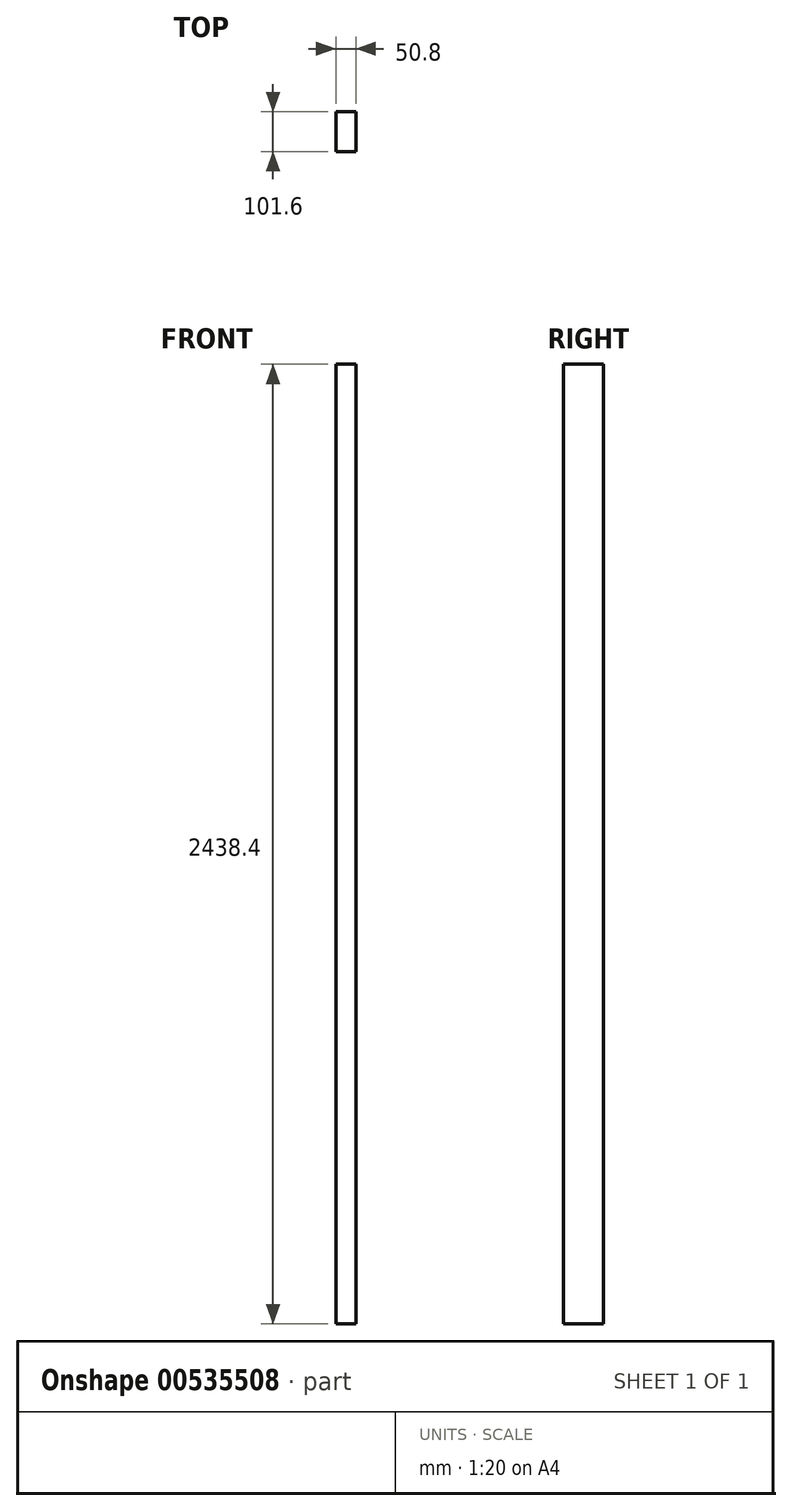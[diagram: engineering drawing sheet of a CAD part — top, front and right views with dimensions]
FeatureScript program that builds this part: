
annotation { "Feature Type Name" : "Feature", "Feature Type Description" : "" }
export const myFeature = defineFeature(function(context is Context, id is Id, definition is map)
    precondition{}
    {
        {
            var Q0;
            Q0=qCreatedBy(makeId("Top.planeOp"),FACE);
            var sketch = newSketch(context, id + "F0", { "sketchPlane" : qUnion([Q0])});
            skLineSegment(sketch, "E0.bottom", {"start": v(-0.98, 9.07) * mm, "end": v(-51.78, 9.07) * mm});
            skLineSegment(sketch, "E0.top", {"start": v(-0.98, 110.67) * mm, "end": v(-51.78, 110.67) * mm});
            skLineSegment(sketch, "E0.left", {"start": v(-0.98, 9.07) * mm, "end": v(-0.98, 110.67) * mm});
            skLineSegment(sketch, "E0.right", {"start": v(-51.78, 9.07) * mm, "end": v(-51.78, 110.67) * mm});
            skSolve(sketch);
        }
        {
            var Q0;
            Q0=makeQuery(id+"F0.imprint","IMPRINT",FACE,{"disambiguationData":[TD([[makeQuery(id+"F0.imprint","IMPRINT",EDGE,{"derivedFrom":sQuery(id+"F0.wireOp",EDGE,"E0.bottom")}),-1.0]])]});
            extrude(context, id + "F1", {"entities" : qUnion([Q0]), "depth" : 2438.4 * mm, "offsetDistance" : 25 * mm});
        }
    });
